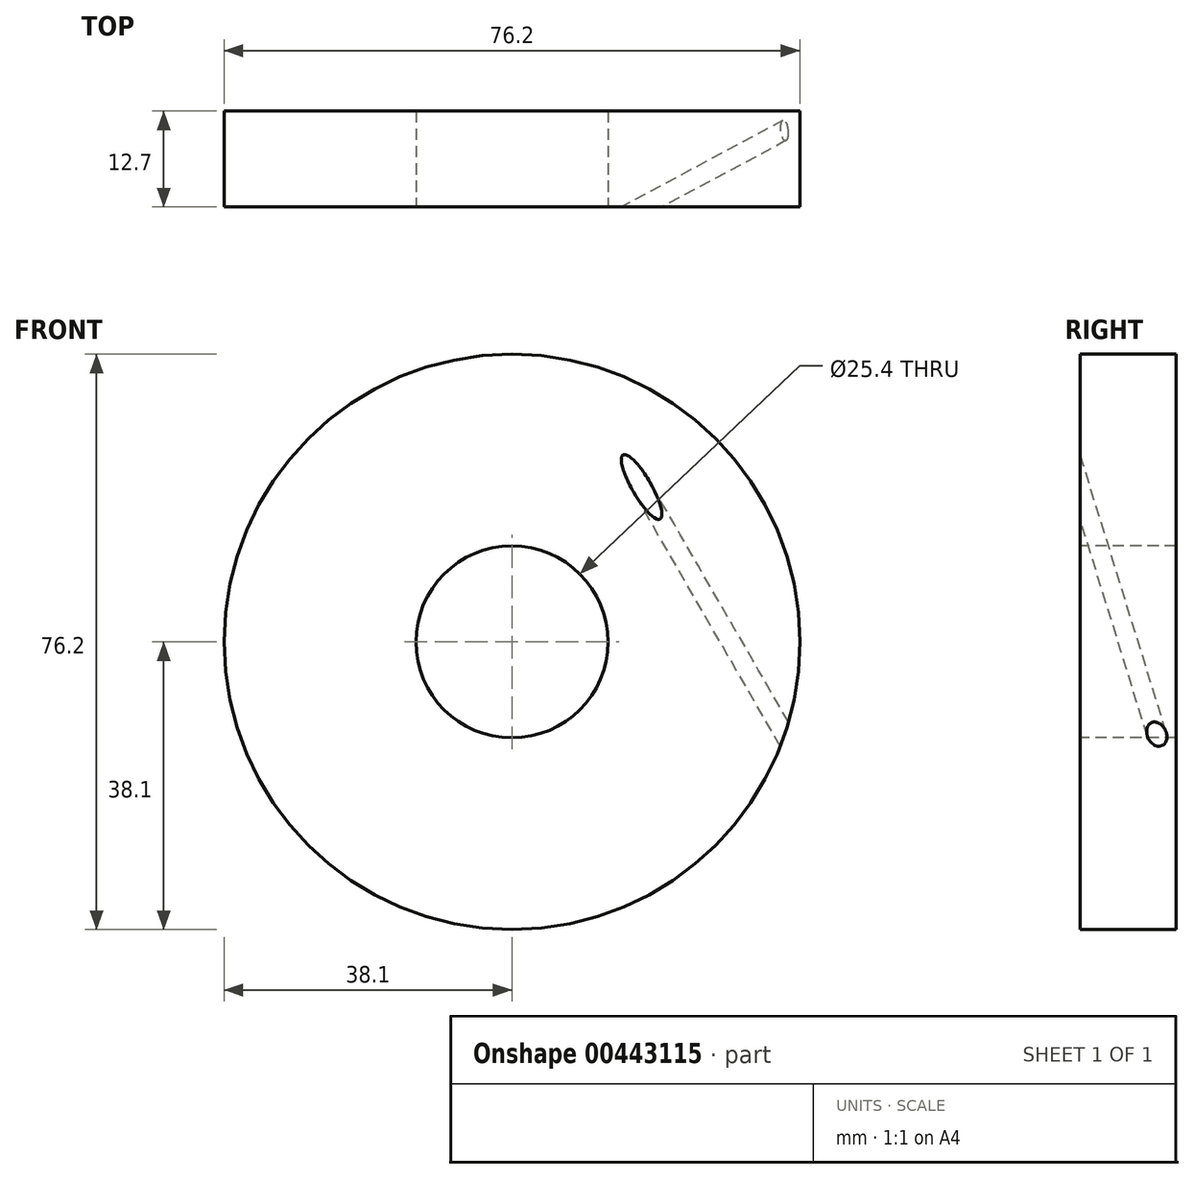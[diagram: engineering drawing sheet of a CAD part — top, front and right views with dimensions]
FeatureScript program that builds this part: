
annotation { "Feature Type Name" : "Feature", "Feature Type Description" : "" }
export const myFeature = defineFeature(function(context is Context, id is Id, definition is map)
    precondition{}
    {
        {
            var Q0;
            Q0=qCreatedBy(makeId("Front.planeOp"),FACE);
            var sketch = newSketch(context, id + "F0", { "sketchPlane" : qUnion([Q0])});
            skCircle(sketch, "E0", {"center": v(0, 0) * mm, "radius": 38.1 * mm});
            skSolve(sketch);
        }
        {
            var Q0;
            Q0=makeQuery(id+"F0.imprint","IMPRINT",FACE,{"disambiguationData":[TD([[makeQuery(id+"F0.imprint","IMPRINT",EDGE,{"derivedFrom":sQuery(id+"F0.wireOp",EDGE,"E0")}),1.0]])]});
            var Q1;
            Q1=sQuery(id+"F0.wireOp",EDGE,"E0");
            extrude(context, id + "F1", {"entities" : qUnion([Q0]), "surfaceEntities" : qUnion([Q1]), "endBound" : BoundingType.SYMMETRIC, "depth" : 12.7 * mm, "offsetDistance" : 25.4 * mm});
        }
        {
            var Q0;
            Q0=makeQuery(id+"F1.opExtrude","CAP_FACE",FACE,{"disambiguationData":[OSD([sQuery(id+"F0.wireOp",EDGE,"E0")])],"isStart":false});
            var sketch = newSketch(context, id + "F2", { "sketchPlane" : qUnion([Q0])});
            skCircle(sketch, "E1", {"center": v(0, 0) * mm, "radius": 12.7 * mm});
            skSolve(sketch);
        }
        {
            var Q0;
            Q0=makeQuery(id+"F2.imprint","IMPRINT",FACE,{"disambiguationData":[TD([[makeQuery(id+"F2.imprint","IMPRINT",EDGE,{"derivedFrom":sQuery(id+"F2.wireOp",EDGE,"E1")}),1.0]])]});
            var Q1;
            Q1=sQuery(id+"F2.wireOp",EDGE,"E1");
            extrude(context, id + "F3", {"entities" : qUnion([Q0]), "operationType" : NewBodyOperationType.REMOVE, "surfaceEntities" : qUnion([Q1]), "oppositeDirection" : true, "depth" : 25.4 * mm, "offsetDistance" : 25.4 * mm});
        }
        {
            var Q0;
            Q0=qCreatedBy(makeId("Top.planeOp"),FACE);
            var sketch = newSketch(context, id + "F4", { "sketchPlane" : qUnion([Q0])});
            skLineSegment(sketch, "E2", {"start": v(0, 0) * mm, "end": v(0, -36.67) * mm});
            skSolve(sketch);
        }
        {
            var Q0;
            Q0=qCreatedBy(makeId("Top.planeOp"),FACE);
            var Q1;
            Q1=sQuery(id+"F4.wireOp",EDGE,"E2");
            cPlane(context, id + "F5", {"entities" : qUnion([Q0, Q1]), "cplaneType" : CPlaneType.LINE_ANGLE, "offset" : 25.4 * mm, "angle" : 30 * degree, "width" : 152.4 * mm, "height" : 152.4 * mm});
        }
        {
            var Q0;
            Q0=qCreatedBy(makeId("Front.planeOp"),FACE);
            var sketch = newSketch(context, id + "F6", { "sketchPlane" : qUnion([Q0])});
            skLineSegment(sketch, "E3", {"start": v(0, 0) * mm, "end": v(51.8, 0) * mm});
            skLineSegment(sketch, "E4", {"start": v(0, 0) * mm, "end": v(47.15, 27.22) * mm});
            skLineSegment(sketch, "E5", {"start": v(0, 0) * mm, "end": v(-19.04, 32.99) * mm});
            skSolve(sketch);
        }
        {
            var Q0;
            Q0=qCreatedBy(id+"F5.planeOp",FACE);
            var Q1;
            Q1=sQuery(id+"F6.wireOp",EDGE,"E4");
            cPlane(context, id + "F7", {"entities" : qUnion([Q0, Q1]), "cplaneType" : CPlaneType.LINE_ANGLE, "offset" : 25.4 * mm, "angle" : 15 * degree, "width" : 152.4 * mm, "height" : 152.4 * mm});
        }
        {
            var Q0;
            Q0=qCreatedBy(id+"F7.planeOp",FACE);
            var sketch = newSketch(context, id + "F8", { "sketchPlane" : qUnion([Q0])});
            skCircle(sketch, "E6", {"center": v(25.4, 0) * mm, "radius": 1.27 * mm});
            skLineSegment(sketch, "E7", {"start": v(0, 0) * mm, "end": v(25.4, 0) * mm, "construction": true});
            skSolve(sketch);
        }
        {
            var Q0;
            Q0 = qSketchRegion(id + "F8", true);
            extrude(context, id + "F9", {"entities" : qUnion([Q0]), "operationType" : NewBodyOperationType.REMOVE, "endBound" : BoundingType.THROUGH_ALL, "oppositeDirection" : true, "depth" : 25.4 * mm, "offsetDistance" : 25.4 * mm, "hasSecondDirection" : true, "secondDirectionBound" : SecondDirectionBoundingType.THROUGH_ALL, "secondDirectionOppositeDirection" : false, "secondDirectionDepth" : 25.4 * mm});
        }
    });
